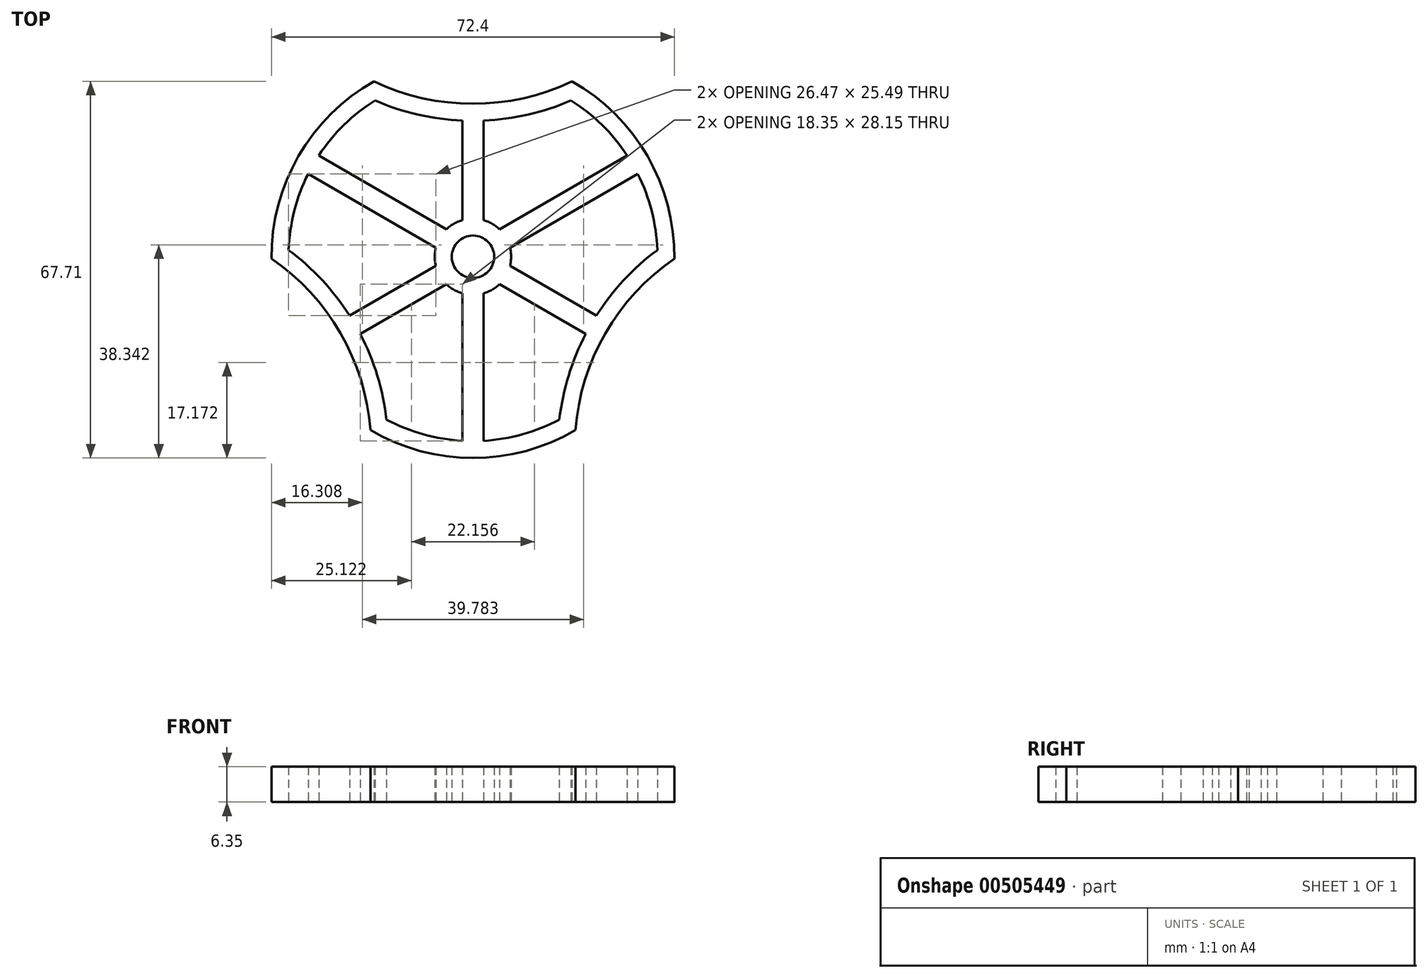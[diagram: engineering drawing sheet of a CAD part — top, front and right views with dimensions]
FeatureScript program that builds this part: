
annotation { "Feature Type Name" : "Feature", "Feature Type Description" : "" }
export const myFeature = defineFeature(function(context is Context, id is Id, definition is map)
    precondition{}
    {
        {
            var Q0;
            Q0=qCreatedBy(makeId("Top.planeOp"),FACE);
            var sketch = newSketch(context, id + "F0", { "sketchPlane" : qUnion([Q0])});
            skCircle(sketch, "E0", {"center": v(0, 0) * mm, "radius": 3.81 * mm});
            skArc(sketch, "E1", {"start": v(-17.79, 31.52) * mm, "mid": v(-31.35, 18.1) * mm, "end": v(-36.2, -0.35) * mm});
            skArc(sketch, "E2", {"start": v(-17.79, 31.52) * mm, "mid": v(0, 27.5) * mm, "end": v(17.79, 31.52) * mm});
            skArc(sketch, "E3.1.0", {"start": v(-18.4, -31.17) * mm, "mid": v(-23.8, -13.75) * mm, "end": v(-36.2, -0.35) * mm});
            skArc(sketch, "E3.2.0", {"start": v(36.2, -0.35) * mm, "mid": v(23.8, -13.75) * mm, "end": v(18.4, -31.17) * mm});
            skArc(sketch, "E4.trimOffspring", {"start": v(-18.4, -31.17) * mm, "mid": v(0, -36.2) * mm, "end": v(18.4, -31.17) * mm});
            skArc(sketch, "E5.trimOffspring", {"start": v(36.2, -0.35) * mm, "mid": v(31.35, 18.1) * mm, "end": v(17.79, 31.52) * mm});
            skPoint(sketch, "E6.center.orphan", {"position": v(-31.35, 18.1) * mm});
            skPoint(sketch, "E7.center.orphan", {"position": v(-35.43, 7.42) * mm});
            skPoint(sketch, "E8.center.orphan", {"position": v(-24.14, 26.97) * mm});
            skLineSegment(sketch, "E9", {"start": v(-29.61, 14.9) * mm, "end": v(-3.8, 0) * mm});
            skLineSegment(sketch, "E10", {"start": v(-27.7, 18.2) * mm, "end": v(-4.75, 4.94) * mm});
            skArc(sketch, "E11.0", {"start": v(-17.6, 28.09) * mm, "mid": v(-23.19, 23.69) * mm, "end": v(-27.7, 18.2) * mm});
            skArc(sketch, "E11.1", {"start": v(33.13, 1.2) * mm, "mid": v(32.1, 8.24) * mm, "end": v(29.61, 14.9) * mm});
            skArc(sketch, "E11.2", {"start": v(33.13, 1.2) * mm, "mid": v(27.1, -4.2) * mm, "end": v(22.16, -10.6) * mm});
            skArc(sketch, "E11.3", {"start": v(-17.6, 28.09) * mm, "mid": v(-9.92, 25.57) * mm, "end": v(-1.9, 24.48) * mm});
            skArc(sketch, "E11.4", {"start": v(-15.52, -29.29) * mm, "mid": v(-8.92, -31.92) * mm, "end": v(-1.9, -33.1) * mm});
            skArc(sketch, "E11.5", {"start": v(-15.52, -29.29) * mm, "mid": v(-17.18, -21.37) * mm, "end": v(-20.25, -13.9) * mm});
            skLineSegment(sketch, "E12.1.0", {"start": v(-1.9, -33.1) * mm, "end": v(-1.9, -6.59) * mm});
            skLineSegment(sketch, "E12.1.1", {"start": v(1.9, -33.1) * mm, "end": v(1.9, -6.59) * mm});
            skLineSegment(sketch, "E12.2.0", {"start": v(29.61, 14.9) * mm, "end": v(6.66, 1.65) * mm});
            skLineSegment(sketch, "E12.2.1", {"start": v(27.7, 18.2) * mm, "end": v(4.75, 4.94) * mm});
            skArc(sketch, "E13.0", {"start": v(1.9, -6.59) * mm, "mid": v(3.43, -5.94) * mm, "end": v(4.75, -4.94) * mm});
            skLineSegment(sketch, "E14", {"start": v(-1.9, 24.48) * mm, "end": v(-1.9, 6.59) * mm});
            skLineSegment(sketch, "E15", {"start": v(1.9, 24.48) * mm, "end": v(1.9, 6.59) * mm});
            skLineSegment(sketch, "E16.1.0", {"start": v(-20.25, -13.9) * mm, "end": v(-4.75, -4.94) * mm});
            skLineSegment(sketch, "E16.1.1", {"start": v(-22.16, -10.6) * mm, "end": v(-6.66, -1.64) * mm});
            skLineSegment(sketch, "E16.2.0", {"start": v(22.16, -10.6) * mm, "end": v(6.66, -1.64) * mm});
            skLineSegment(sketch, "E16.2.1", {"start": v(20.25, -13.9) * mm, "end": v(4.75, -4.94) * mm});
            skPoint(sketch, "E17.orphan", {"position": v(-30.35, 19.72) * mm});
            skPoint(sketch, "E18.orphan", {"position": v(-32.3, 16.45) * mm});
            skArc(sketch, "E19.trimOffspring", {"start": v(20.25, -13.9) * mm, "mid": v(17.18, -21.37) * mm, "end": v(15.52, -29.29) * mm});
            skArc(sketch, "E20.trimOffspring", {"start": v(27.7, 18.2) * mm, "mid": v(23.19, 23.69) * mm, "end": v(17.6, 28.09) * mm});
            skArc(sketch, "E21.trimOffspring", {"start": v(1.9, 24.48) * mm, "mid": v(9.92, 25.57) * mm, "end": v(17.6, 28.09) * mm});
            skArc(sketch, "E22.trimOffspring", {"start": v(-29.61, 14.9) * mm, "mid": v(-32.1, 8.24) * mm, "end": v(-33.13, 1.2) * mm});
            skArc(sketch, "E23.trimOffspring", {"start": v(-22.16, -10.6) * mm, "mid": v(-27.1, -4.2) * mm, "end": v(-33.13, 1.2) * mm});
            skPoint(sketch, "E24.orphan", {"position": v(1.9, -36.2) * mm});
            skPoint(sketch, "E25.orphan", {"position": v(-1.9, -36.14) * mm});
            skArc(sketch, "E26.trimOffspring", {"start": v(1.9, -33.1) * mm, "mid": v(8.92, -31.92) * mm, "end": v(15.52, -29.29) * mm});
            skPoint(sketch, "E27.orphan", {"position": v(-1.9, 3.3) * mm});
            skArc(sketch, "E28.trimOffspring", {"start": v(-1.9, 6.59) * mm, "mid": v(-3.43, 5.94) * mm, "end": v(-4.75, 4.94) * mm});
            skArc(sketch, "E29.trimOffspring", {"start": v(-6.66, 1.64) * mm, "mid": v(-6.86, 0) * mm, "end": v(-6.66, -1.64) * mm});
            skArc(sketch, "E30.trimOffspring", {"start": v(6.66, -1.64) * mm, "mid": v(6.86, 0) * mm, "end": v(6.66, 1.65) * mm});
            skArc(sketch, "E31.trimOffspring", {"start": v(4.75, 4.94) * mm, "mid": v(3.43, 5.94) * mm, "end": v(1.9, 6.59) * mm});
            skPoint(sketch, "E32.orphan", {"position": v(1.9, -3.3) * mm});
            skPoint(sketch, "E33.orphan", {"position": v(-1.9, -3.3) * mm});
            skPoint(sketch, "E34.orphan", {"position": v(1.9, 3.3) * mm});
            skPoint(sketch, "E35.orphan", {"position": v(3.8, 0) * mm});
            skArc(sketch, "E36", {"start": v(-4.75, -4.94) * mm, "mid": v(-3.43, -5.94) * mm, "end": v(-1.9, -6.59) * mm});
            skPoint(sketch, "E37.orphan", {"position": v(30.4, 19.75) * mm});
            skPoint(sketch, "E38.orphan", {"position": v(32.25, 16.42) * mm});
            skSolve(sketch);
        }
        {
            var Q0;
            Q0=qSketchRegion(id+"F0",true);
            extrude(context, id + "F1", {"entities" : qUnion([Q0]), "depth" : 6.35 * mm, "offsetDistance" : 25.4 * mm});
        }
    });
